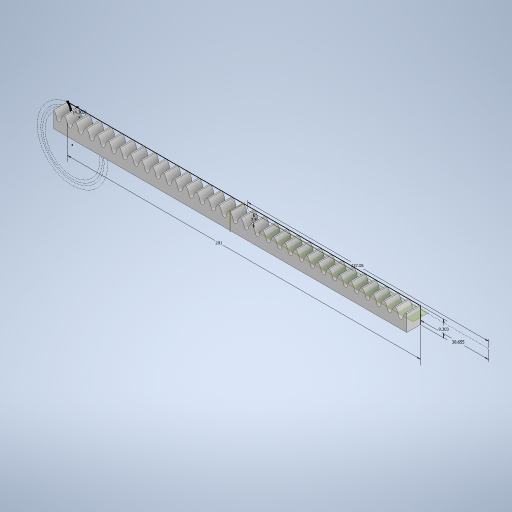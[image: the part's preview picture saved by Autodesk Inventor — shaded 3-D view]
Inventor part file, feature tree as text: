
AUTODESK INVENTOR PART (.ipt)
format: ipt  version: 2023 (Build 270158000, 158)  size: 421,888 bytes
history: native  units: mm
features: extrude x2, plane x2, other x1, sketch x1, pattern_linear x1, split x1
ambient origin geometry x8: Origin, YZ Plane, XZ Plane, XY Plane, X Axis, Y Axis, Z Axis, Center Point
bodies: Solid3 (feature_tree), Solid4 (feature_tree)
feature tree (8):
  other  "pinion"
  sketch  "Sketch1"  dims[d2=9.303mm d3=201.0mm d4=4.303311mm d5=7.82mm d6=0.0mm d7=0.0mm d8=0.0mm d9=320.0mm d11=6.28mm d12=137.050182mm d14=90.0deg d15=38.65503mm d16=7.499689mm d17=-100.5mm]
  extrude  "Extrusion2"  Depth=201.0mm
  extrude  "Extrusion3"  Depth=4.303311mm
  pattern_linear  "Rectangular Pattern1"  Spacing1=7.82mm  [1 undecoded]
  plane  "Work Plane1"
  plane  "Work Plane2"
  split  "Split1"
note: 1 required parameter value undecoded (feature->parameter linkage not recoverable at this tier; creation-order binding heuristic only, values carry confidence <= 0.55)
